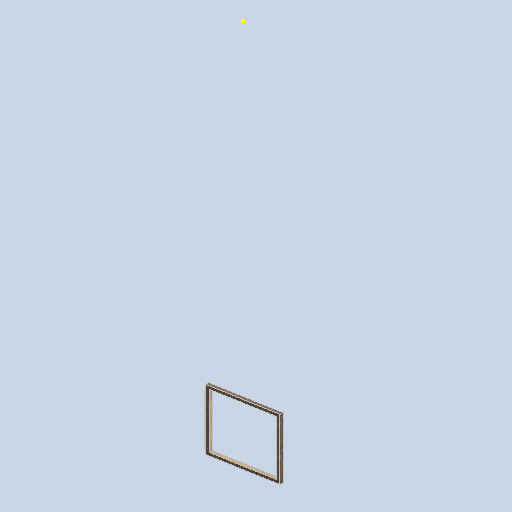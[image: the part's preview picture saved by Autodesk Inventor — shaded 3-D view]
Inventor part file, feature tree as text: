
AUTODESK INVENTOR PART (.ipt)
format: ipt  version: 2024.2 (Build 282272000, 272)  size: 124,416 bytes
history: native  units: in
note: dims shown in document units (in); Inventor stores cm internally (conversion verified against a paired STEP export)
features: sketch x9, plane x4, other x3
ambient origin geometry x8: Origin, YZ Plane, XZ Plane, XY Plane, X Axis, Y Axis, Z Axis, Center Point
bodies: Solid1 (feature_tree)
feature tree (16):
  other  "eave_frame_side_MIR.ipt"
  other  "Solid1::eave_frame_side_MIR.ipt"
  other  "TaggingFeature1"
  sketch  "Sketch1"  dims[d0=0.3937in]
  sketch  "Sketch2"
  sketch  "Sketch3"
  sketch  "Sketch4"
  sketch  "Sketch5"
  sketch  "Sketch6"
  sketch  "Sketch7"
  sketch  "Sketch8"
  sketch  "Sketch9"
  plane  "Work Plane1"
  plane  "Work Plane2"
  plane  "Work Plane3"
  plane  "Work Plane4"
